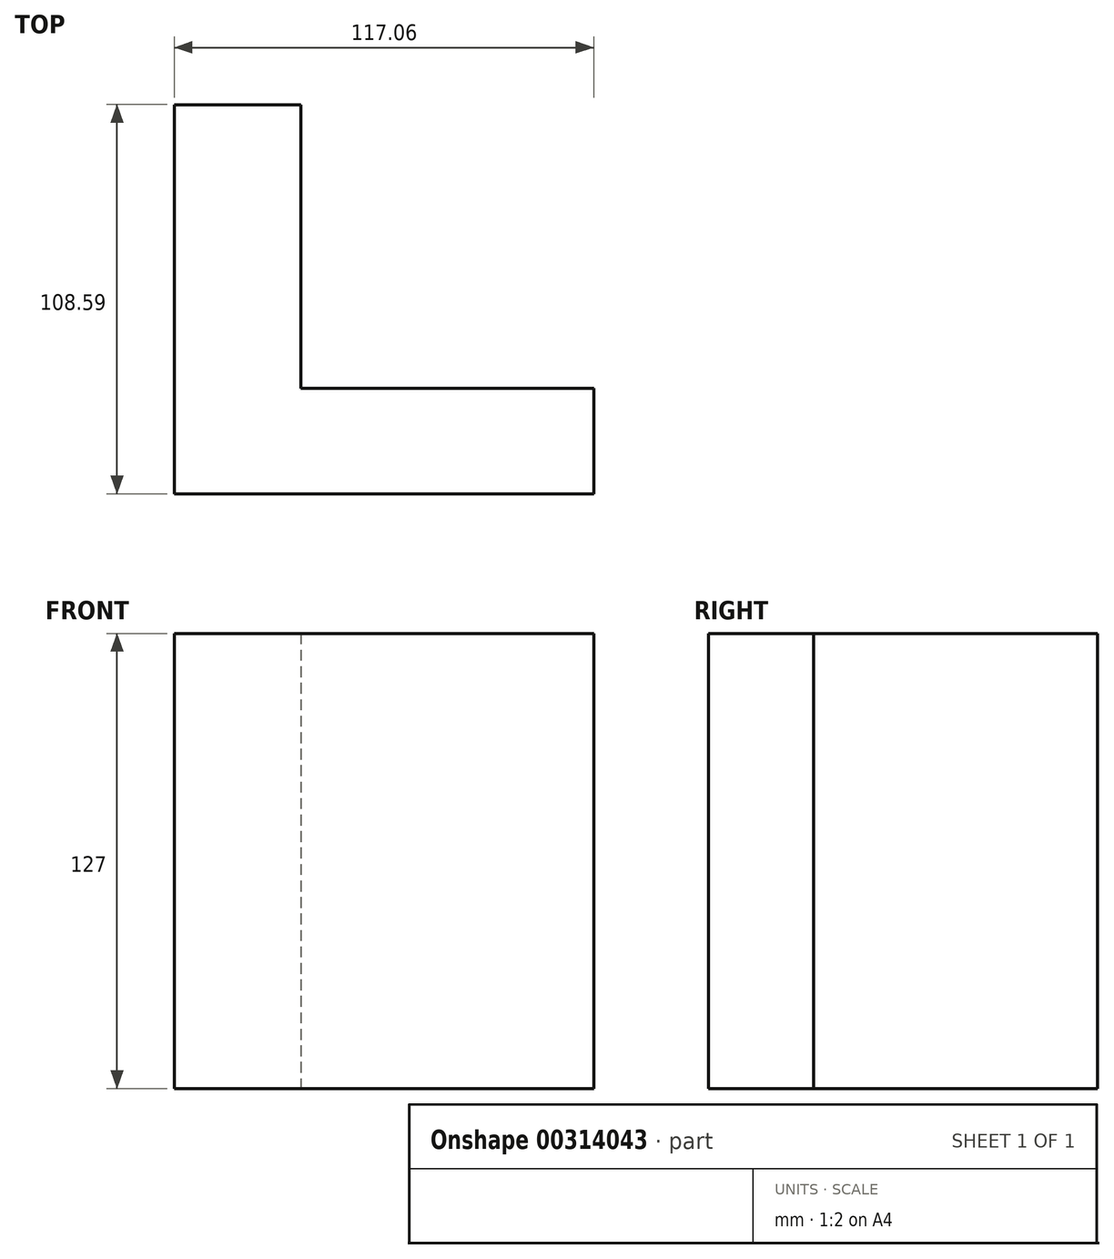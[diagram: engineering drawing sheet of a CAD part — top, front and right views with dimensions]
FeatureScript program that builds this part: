
annotation { "Feature Type Name" : "Feature", "Feature Type Description" : "" }
export const myFeature = defineFeature(function(context is Context, id is Id, definition is map)
    precondition{}
    {
        {
            var Q0;
            Q0=qCreatedBy(makeId("Top.planeOp"),FACE);
            var sketch = newSketch(context, id + "F0", { "sketchPlane" : qUnion([Q0])});
            skLineSegment(sketch, "E0", {"start": v(-56.76, 47.89) * mm, "end": v(-56.76, -60.7) * mm});
            skLineSegment(sketch, "E1", {"start": v(-56.76, -60.7) * mm, "end": v(60.3, -60.7) * mm});
            skLineSegment(sketch, "E2", {"start": v(60.3, -60.7) * mm, "end": v(60.3, -31.33) * mm});
            skLineSegment(sketch, "E3", {"start": v(60.3, -31.33) * mm, "end": v(-21.48, -31.33) * mm});
            skLineSegment(sketch, "E4", {"start": v(-21.48, -31.33) * mm, "end": v(-21.48, 47.89) * mm});
            skLineSegment(sketch, "E5", {"start": v(-21.48, 47.89) * mm, "end": v(-56.76, 47.89) * mm});
            skSolve(sketch);
        }
        {
            var Q0;
            Q0 = qSketchRegion(id + "F0", true);
            extrude(context, id + "F1", {"entities" : qUnion([Q0]), "depth" : 127 * mm});
        }
    });
